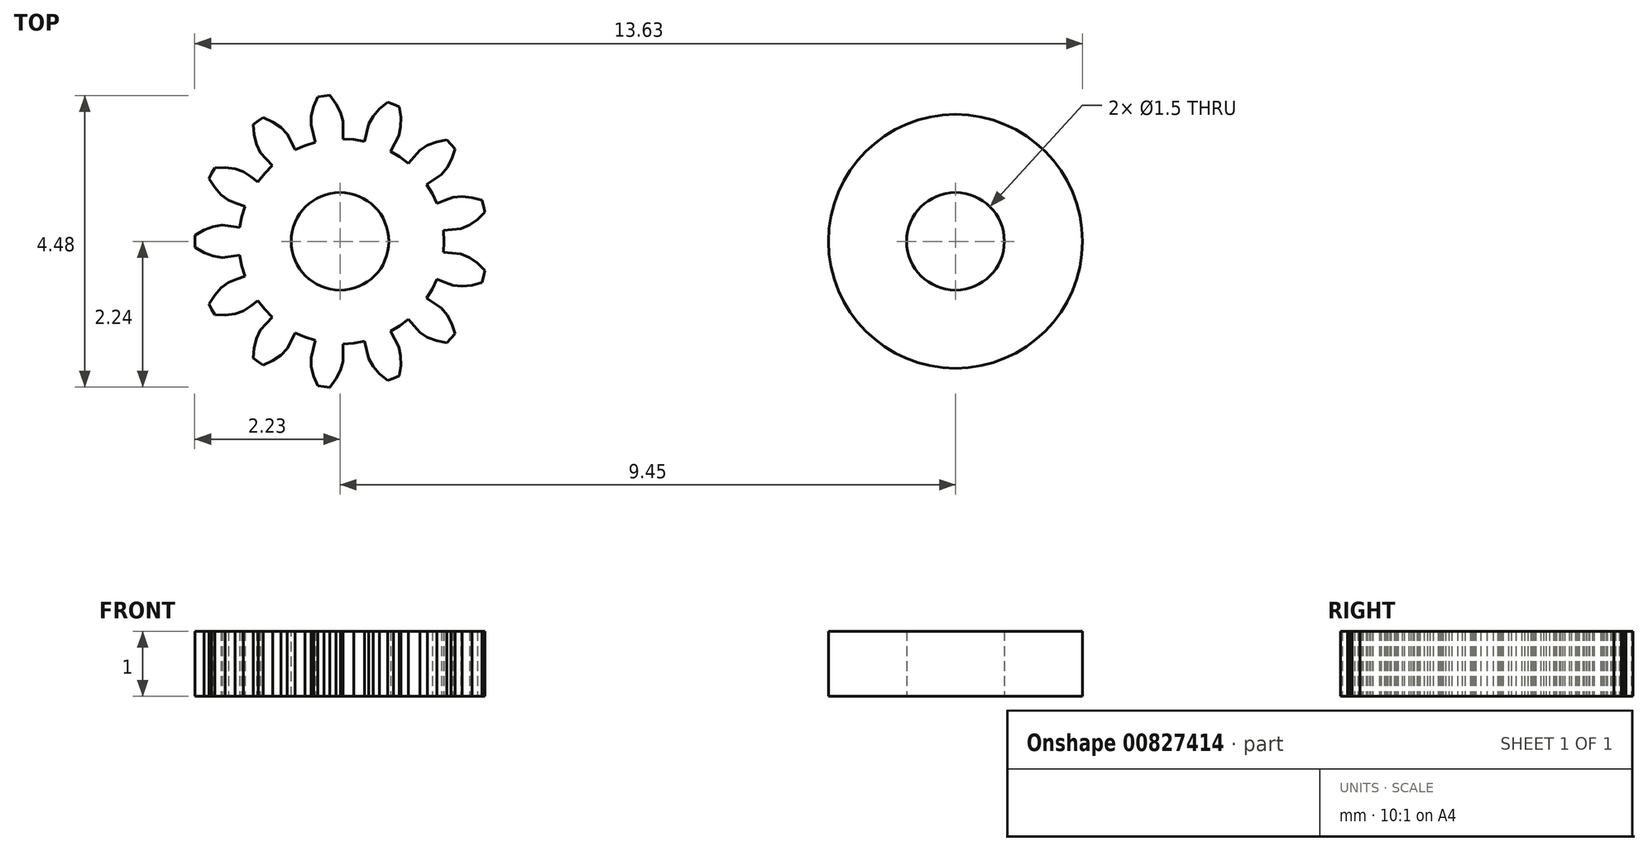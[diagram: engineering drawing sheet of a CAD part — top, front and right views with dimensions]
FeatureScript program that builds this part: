
annotation { "Feature Type Name" : "Feature", "Feature Type Description" : "" }
export const myFeature = defineFeature(function(context is Context, id is Id, definition is map)
    precondition{}
    {
        {
            var Q0;
            Q0=qCreatedBy(makeId("Top.planeOp"),FACE);
            var sketch = newSketch(context, id + "F0", { "sketchPlane" : qUnion([Q0])});
            skLineSegment(sketch, "E0", {"start": v(1.6, 0) * mm, "end": v(1.59, 0.17) * mm});
            skLineSegment(sketch, "E1", {"start": v(1.59, 0.17) * mm, "end": v(1.72, 0.18) * mm});
            skLineSegment(sketch, "E2", {"start": v(1.72, 0.18) * mm, "end": v(1.86, 0.2) * mm});
            skLineSegment(sketch, "E3", {"start": v(1.86, 0.2) * mm, "end": v(1.99, 0.25) * mm});
            skLineSegment(sketch, "E4", {"start": v(1.99, 0.25) * mm, "end": v(2.11, 0.34) * mm});
            skLineSegment(sketch, "E5", {"start": v(2.11, 0.34) * mm, "end": v(2.23, 0.45) * mm});
            skLineSegment(sketch, "E6", {"start": v(2.23, 0.45) * mm, "end": v(2.2, 0.54) * mm});
            skLineSegment(sketch, "E7", {"start": v(2.2, 0.54) * mm, "end": v(2.18, 0.63) * mm});
            skLineSegment(sketch, "E8", {"start": v(2.18, 0.63) * mm, "end": v(2.03, 0.67) * mm});
            skLineSegment(sketch, "E9", {"start": v(2.03, 0.67) * mm, "end": v(1.88, 0.7) * mm});
            skLineSegment(sketch, "E10", {"start": v(1.88, 0.7) * mm, "end": v(1.74, 0.68) * mm});
            skLineSegment(sketch, "E11", {"start": v(1.74, 0.68) * mm, "end": v(1.61, 0.63) * mm});
            skLineSegment(sketch, "E12", {"start": v(1.61, 0.63) * mm, "end": v(1.49, 0.58) * mm});
            skLineSegment(sketch, "E13", {"start": v(1.49, 0.58) * mm, "end": v(1.42, 0.73) * mm});
            skLineSegment(sketch, "E14", {"start": v(1.42, 0.73) * mm, "end": v(1.33, 0.88) * mm});
            skLineSegment(sketch, "E15", {"start": v(1.33, 0.88) * mm, "end": v(1.44, 0.95) * mm});
            skLineSegment(sketch, "E16", {"start": v(1.44, 0.95) * mm, "end": v(1.56, 1.03) * mm});
            skLineSegment(sketch, "E17", {"start": v(1.56, 1.03) * mm, "end": v(1.65, 1.13) * mm});
            skLineSegment(sketch, "E18", {"start": v(1.65, 1.13) * mm, "end": v(1.72, 1.27) * mm});
            skLineSegment(sketch, "E19", {"start": v(1.72, 1.27) * mm, "end": v(1.77, 1.42) * mm});
            skLineSegment(sketch, "E20", {"start": v(1.77, 1.42) * mm, "end": v(1.7, 1.5) * mm});
            skLineSegment(sketch, "E21", {"start": v(1.7, 1.5) * mm, "end": v(1.64, 1.56) * mm});
            skLineSegment(sketch, "E22", {"start": v(1.64, 1.56) * mm, "end": v(1.48, 1.53) * mm});
            skLineSegment(sketch, "E23", {"start": v(1.48, 1.53) * mm, "end": v(1.34, 1.47) * mm});
            skLineSegment(sketch, "E24", {"start": v(1.34, 1.47) * mm, "end": v(1.23, 1.4) * mm});
            skLineSegment(sketch, "E25", {"start": v(1.23, 1.4) * mm, "end": v(1.14, 1.3) * mm});
            skLineSegment(sketch, "E26", {"start": v(1.14, 1.3) * mm, "end": v(1.05, 1.2) * mm});
            skLineSegment(sketch, "E27", {"start": v(1.05, 1.2) * mm, "end": v(0.92, 1.3) * mm});
            skLineSegment(sketch, "E28", {"start": v(0.92, 1.3) * mm, "end": v(0.77, 1.38) * mm});
            skLineSegment(sketch, "E29", {"start": v(0.77, 1.38) * mm, "end": v(0.84, 1.5) * mm});
            skLineSegment(sketch, "E30", {"start": v(0.84, 1.5) * mm, "end": v(0.9, 1.62) * mm});
            skLineSegment(sketch, "E31", {"start": v(0.9, 1.62) * mm, "end": v(0.93, 1.76) * mm});
            skLineSegment(sketch, "E32", {"start": v(0.93, 1.76) * mm, "end": v(0.93, 1.9) * mm});
            skLineSegment(sketch, "E33", {"start": v(0.93, 1.9) * mm, "end": v(0.9, 2.07) * mm});
            skLineSegment(sketch, "E34", {"start": v(0.9, 2.07) * mm, "end": v(0.82, 2.1) * mm});
            skLineSegment(sketch, "E35", {"start": v(0.82, 2.1) * mm, "end": v(0.73, 2.14) * mm});
            skLineSegment(sketch, "E36", {"start": v(0.73, 2.14) * mm, "end": v(0.6, 2.03) * mm});
            skLineSegment(sketch, "E37", {"start": v(0.6, 2.03) * mm, "end": v(0.5, 1.92) * mm});
            skLineSegment(sketch, "E38", {"start": v(0.5, 1.92) * mm, "end": v(0.44, 1.8) * mm});
            skLineSegment(sketch, "E39", {"start": v(0.44, 1.8) * mm, "end": v(0.4, 1.67) * mm});
            skLineSegment(sketch, "E40", {"start": v(0.4, 1.67) * mm, "end": v(0.38, 1.53) * mm});
            skLineSegment(sketch, "E41", {"start": v(0.38, 1.53) * mm, "end": v(0.21, 1.56) * mm});
            skLineSegment(sketch, "E42", {"start": v(0.21, 1.56) * mm, "end": v(0.05, 1.57) * mm});
            skLineSegment(sketch, "E43", {"start": v(0.05, 1.57) * mm, "end": v(0.05, 1.7) * mm});
            skLineSegment(sketch, "E44", {"start": v(0.05, 1.7) * mm, "end": v(0.05, 1.84) * mm});
            skLineSegment(sketch, "E45", {"start": v(0.05, 1.84) * mm, "end": v(0.01, 1.98) * mm});
            skLineSegment(sketch, "E46", {"start": v(0.01, 1.98) * mm, "end": v(-0.06, 2.11) * mm});
            skLineSegment(sketch, "E47", {"start": v(-0.06, 2.11) * mm, "end": v(-0.15, 2.24) * mm});
            skLineSegment(sketch, "E48", {"start": v(-0.15, 2.24) * mm, "end": v(-0.25, 2.23) * mm});
            skLineSegment(sketch, "E49", {"start": v(-0.25, 2.23) * mm, "end": v(-0.34, 2.22) * mm});
            skLineSegment(sketch, "E50", {"start": v(-0.34, 2.22) * mm, "end": v(-0.4, 2.07) * mm});
            skLineSegment(sketch, "E51", {"start": v(-0.4, 2.07) * mm, "end": v(-0.44, 1.93) * mm});
            skLineSegment(sketch, "E52", {"start": v(-0.44, 1.93) * mm, "end": v(-0.44, 1.78) * mm});
            skLineSegment(sketch, "E53", {"start": v(-0.44, 1.78) * mm, "end": v(-0.41, 1.65) * mm});
            skLineSegment(sketch, "E54", {"start": v(-0.41, 1.65) * mm, "end": v(-0.38, 1.52) * mm});
            skLineSegment(sketch, "E55", {"start": v(-0.38, 1.52) * mm, "end": v(-0.54, 1.47) * mm});
            skLineSegment(sketch, "E56", {"start": v(-0.54, 1.47) * mm, "end": v(-0.69, 1.4) * mm});
            skLineSegment(sketch, "E57", {"start": v(-0.69, 1.4) * mm, "end": v(-0.75, 1.53) * mm});
            skLineSegment(sketch, "E58", {"start": v(-0.75, 1.53) * mm, "end": v(-0.81, 1.65) * mm});
            skLineSegment(sketch, "E59", {"start": v(-0.81, 1.65) * mm, "end": v(-0.9, 1.75) * mm});
            skLineSegment(sketch, "E60", {"start": v(-0.9, 1.75) * mm, "end": v(-1.03, 1.83) * mm});
            skLineSegment(sketch, "E61", {"start": v(-1.03, 1.83) * mm, "end": v(-1.18, 1.9) * mm});
            skLineSegment(sketch, "E62", {"start": v(-1.18, 1.9) * mm, "end": v(-1.26, 1.85) * mm});
            skLineSegment(sketch, "E63", {"start": v(-1.26, 1.85) * mm, "end": v(-1.33, 1.8) * mm});
            skLineSegment(sketch, "E64", {"start": v(-1.33, 1.8) * mm, "end": v(-1.32, 1.64) * mm});
            skLineSegment(sketch, "E65", {"start": v(-1.32, 1.64) * mm, "end": v(-1.28, 1.49) * mm});
            skLineSegment(sketch, "E66", {"start": v(-1.28, 1.49) * mm, "end": v(-1.22, 1.36) * mm});
            skLineSegment(sketch, "E67", {"start": v(-1.22, 1.36) * mm, "end": v(-1.13, 1.26) * mm});
            skLineSegment(sketch, "E68", {"start": v(-1.13, 1.26) * mm, "end": v(-1.04, 1.16) * mm});
            skLineSegment(sketch, "E69", {"start": v(-1.04, 1.16) * mm, "end": v(-1.16, 1.04) * mm});
            skLineSegment(sketch, "E70", {"start": v(-1.16, 1.04) * mm, "end": v(-1.26, 0.91) * mm});
            skLineSegment(sketch, "E71", {"start": v(-1.26, 0.91) * mm, "end": v(-1.37, 1) * mm});
            skLineSegment(sketch, "E72", {"start": v(-1.37, 1) * mm, "end": v(-1.48, 1.07) * mm});
            skLineSegment(sketch, "E73", {"start": v(-1.48, 1.07) * mm, "end": v(-1.61, 1.12) * mm});
            skLineSegment(sketch, "E74", {"start": v(-1.61, 1.12) * mm, "end": v(-1.76, 1.13) * mm});
            skLineSegment(sketch, "E75", {"start": v(-1.76, 1.13) * mm, "end": v(-1.92, 1.13) * mm});
            skLineSegment(sketch, "E76", {"start": v(-1.92, 1.13) * mm, "end": v(-1.97, 1.05) * mm});
            skLineSegment(sketch, "E77", {"start": v(-1.97, 1.05) * mm, "end": v(-2.01, 0.96) * mm});
            skLineSegment(sketch, "E78", {"start": v(-2.01, 0.96) * mm, "end": v(-1.92, 0.83) * mm});
            skLineSegment(sketch, "E79", {"start": v(-1.92, 0.83) * mm, "end": v(-1.82, 0.71) * mm});
            skLineSegment(sketch, "E80", {"start": v(-1.82, 0.71) * mm, "end": v(-1.71, 0.63) * mm});
            skLineSegment(sketch, "E81", {"start": v(-1.71, 0.63) * mm, "end": v(-1.59, 0.58) * mm});
            skLineSegment(sketch, "E82", {"start": v(-1.59, 0.58) * mm, "end": v(-1.46, 0.54) * mm});
            skLineSegment(sketch, "E83", {"start": v(-1.46, 0.54) * mm, "end": v(-1.5, 0.38) * mm});
            skLineSegment(sketch, "E84", {"start": v(-1.5, 0.38) * mm, "end": v(-1.54, 0.21) * mm});
            skLineSegment(sketch, "E85", {"start": v(-1.54, 0.21) * mm, "end": v(-1.67, 0.23) * mm});
            skLineSegment(sketch, "E86", {"start": v(-1.67, 0.23) * mm, "end": v(-1.8, 0.25) * mm});
            skLineSegment(sketch, "E87", {"start": v(-1.8, 0.25) * mm, "end": v(-1.94, 0.23) * mm});
            skLineSegment(sketch, "E88", {"start": v(-1.94, 0.23) * mm, "end": v(-2.09, 0.17) * mm});
            skLineSegment(sketch, "E89", {"start": v(-2.09, 0.17) * mm, "end": v(-2.23, 0.1) * mm});
            skLineSegment(sketch, "E90", {"start": v(-2.23, 0.1) * mm, "end": v(-2.23, 0) * mm});
            skLineSegment(sketch, "E91", {"start": v(-2.23, 0) * mm, "end": v(-2.23, -0.1) * mm});
            skLineSegment(sketch, "E92", {"start": v(-2.23, -0.1) * mm, "end": v(-2.09, -0.17) * mm});
            skLineSegment(sketch, "E93", {"start": v(-2.09, -0.17) * mm, "end": v(-1.94, -0.23) * mm});
            skLineSegment(sketch, "E94", {"start": v(-1.94, -0.23) * mm, "end": v(-1.8, -0.25) * mm});
            skLineSegment(sketch, "E95", {"start": v(-1.8, -0.25) * mm, "end": v(-1.67, -0.23) * mm});
            skLineSegment(sketch, "E96", {"start": v(-1.67, -0.23) * mm, "end": v(-1.54, -0.21) * mm});
            skLineSegment(sketch, "E97", {"start": v(-1.54, -0.21) * mm, "end": v(-1.5, -0.38) * mm});
            skLineSegment(sketch, "E98", {"start": v(-1.5, -0.38) * mm, "end": v(-1.46, -0.54) * mm});
            skLineSegment(sketch, "E99", {"start": v(-1.46, -0.54) * mm, "end": v(-1.59, -0.58) * mm});
            skLineSegment(sketch, "E100", {"start": v(-1.59, -0.58) * mm, "end": v(-1.71, -0.63) * mm});
            skLineSegment(sketch, "E101", {"start": v(-1.71, -0.63) * mm, "end": v(-1.82, -0.71) * mm});
            skLineSegment(sketch, "E102", {"start": v(-1.82, -0.71) * mm, "end": v(-1.92, -0.83) * mm});
            skLineSegment(sketch, "E103", {"start": v(-1.92, -0.83) * mm, "end": v(-2.01, -0.96) * mm});
            skLineSegment(sketch, "E104", {"start": v(-2.01, -0.96) * mm, "end": v(-1.97, -1.05) * mm});
            skLineSegment(sketch, "E105", {"start": v(-1.97, -1.05) * mm, "end": v(-1.92, -1.13) * mm});
            skLineSegment(sketch, "E106", {"start": v(-1.92, -1.13) * mm, "end": v(-1.76, -1.13) * mm});
            skLineSegment(sketch, "E107", {"start": v(-1.76, -1.13) * mm, "end": v(-1.61, -1.12) * mm});
            skLineSegment(sketch, "E108", {"start": v(-1.61, -1.12) * mm, "end": v(-1.48, -1.07) * mm});
            skLineSegment(sketch, "E109", {"start": v(-1.48, -1.07) * mm, "end": v(-1.37, -1) * mm});
            skLineSegment(sketch, "E110", {"start": v(-1.37, -1) * mm, "end": v(-1.26, -0.91) * mm});
            skLineSegment(sketch, "E111", {"start": v(-1.26, -0.91) * mm, "end": v(-1.16, -1.04) * mm});
            skLineSegment(sketch, "E112", {"start": v(-1.16, -1.04) * mm, "end": v(-1.04, -1.16) * mm});
            skLineSegment(sketch, "E113", {"start": v(-1.04, -1.16) * mm, "end": v(-1.13, -1.26) * mm});
            skLineSegment(sketch, "E114", {"start": v(-1.13, -1.26) * mm, "end": v(-1.22, -1.36) * mm});
            skLineSegment(sketch, "E115", {"start": v(-1.22, -1.36) * mm, "end": v(-1.28, -1.49) * mm});
            skLineSegment(sketch, "E116", {"start": v(-1.28, -1.49) * mm, "end": v(-1.32, -1.64) * mm});
            skLineSegment(sketch, "E117", {"start": v(-1.32, -1.64) * mm, "end": v(-1.33, -1.8) * mm});
            skLineSegment(sketch, "E118", {"start": v(-1.33, -1.8) * mm, "end": v(-1.26, -1.85) * mm});
            skLineSegment(sketch, "E119", {"start": v(-1.26, -1.85) * mm, "end": v(-1.18, -1.9) * mm});
            skLineSegment(sketch, "E120", {"start": v(-1.18, -1.9) * mm, "end": v(-1.03, -1.83) * mm});
            skLineSegment(sketch, "E121", {"start": v(-1.03, -1.83) * mm, "end": v(-0.9, -1.75) * mm});
            skLineSegment(sketch, "E122", {"start": v(-0.9, -1.75) * mm, "end": v(-0.81, -1.65) * mm});
            skLineSegment(sketch, "E123", {"start": v(-0.81, -1.65) * mm, "end": v(-0.75, -1.53) * mm});
            skLineSegment(sketch, "E124", {"start": v(-0.75, -1.53) * mm, "end": v(-0.69, -1.4) * mm});
            skLineSegment(sketch, "E125", {"start": v(-0.69, -1.4) * mm, "end": v(-0.54, -1.47) * mm});
            skLineSegment(sketch, "E126", {"start": v(-0.54, -1.47) * mm, "end": v(-0.38, -1.52) * mm});
            skLineSegment(sketch, "E127", {"start": v(-0.38, -1.52) * mm, "end": v(-0.41, -1.65) * mm});
            skLineSegment(sketch, "E128", {"start": v(-0.41, -1.65) * mm, "end": v(-0.44, -1.78) * mm});
            skLineSegment(sketch, "E129", {"start": v(-0.44, -1.78) * mm, "end": v(-0.44, -1.93) * mm});
            skLineSegment(sketch, "E130", {"start": v(-0.44, -1.93) * mm, "end": v(-0.4, -2.07) * mm});
            skLineSegment(sketch, "E131", {"start": v(-0.4, -2.07) * mm, "end": v(-0.34, -2.22) * mm});
            skLineSegment(sketch, "E132", {"start": v(-0.34, -2.22) * mm, "end": v(-0.25, -2.23) * mm});
            skLineSegment(sketch, "E133", {"start": v(-0.25, -2.23) * mm, "end": v(-0.15, -2.24) * mm});
            skLineSegment(sketch, "E134", {"start": v(-0.15, -2.24) * mm, "end": v(-0.06, -2.11) * mm});
            skLineSegment(sketch, "E135", {"start": v(-0.06, -2.11) * mm, "end": v(0.01, -1.98) * mm});
            skLineSegment(sketch, "E136", {"start": v(0.01, -1.98) * mm, "end": v(0.05, -1.84) * mm});
            skLineSegment(sketch, "E137", {"start": v(0.05, -1.84) * mm, "end": v(0.05, -1.7) * mm});
            skLineSegment(sketch, "E138", {"start": v(0.05, -1.7) * mm, "end": v(0.05, -1.57) * mm});
            skLineSegment(sketch, "E139", {"start": v(0.05, -1.57) * mm, "end": v(0.21, -1.56) * mm});
            skLineSegment(sketch, "E140", {"start": v(0.21, -1.56) * mm, "end": v(0.38, -1.53) * mm});
            skLineSegment(sketch, "E141", {"start": v(0.38, -1.53) * mm, "end": v(0.4, -1.67) * mm});
            skLineSegment(sketch, "E142", {"start": v(0.4, -1.67) * mm, "end": v(0.44, -1.8) * mm});
            skLineSegment(sketch, "E143", {"start": v(0.44, -1.8) * mm, "end": v(0.5, -1.92) * mm});
            skLineSegment(sketch, "E144", {"start": v(0.5, -1.92) * mm, "end": v(0.6, -2.03) * mm});
            skLineSegment(sketch, "E145", {"start": v(0.6, -2.03) * mm, "end": v(0.73, -2.14) * mm});
            skLineSegment(sketch, "E146", {"start": v(0.73, -2.14) * mm, "end": v(0.82, -2.1) * mm});
            skLineSegment(sketch, "E147", {"start": v(0.82, -2.1) * mm, "end": v(0.9, -2.07) * mm});
            skLineSegment(sketch, "E148", {"start": v(0.9, -2.07) * mm, "end": v(0.93, -1.9) * mm});
            skLineSegment(sketch, "E149", {"start": v(0.93, -1.9) * mm, "end": v(0.93, -1.76) * mm});
            skLineSegment(sketch, "E150", {"start": v(0.93, -1.76) * mm, "end": v(0.9, -1.62) * mm});
            skLineSegment(sketch, "E151", {"start": v(0.9, -1.62) * mm, "end": v(0.84, -1.5) * mm});
            skLineSegment(sketch, "E152", {"start": v(0.84, -1.5) * mm, "end": v(0.77, -1.38) * mm});
            skLineSegment(sketch, "E153", {"start": v(0.77, -1.38) * mm, "end": v(0.92, -1.3) * mm});
            skLineSegment(sketch, "E154", {"start": v(0.92, -1.3) * mm, "end": v(1.05, -1.2) * mm});
            skLineSegment(sketch, "E155", {"start": v(1.05, -1.2) * mm, "end": v(1.14, -1.3) * mm});
            skLineSegment(sketch, "E156", {"start": v(1.14, -1.3) * mm, "end": v(1.23, -1.4) * mm});
            skLineSegment(sketch, "E157", {"start": v(1.23, -1.4) * mm, "end": v(1.34, -1.47) * mm});
            skLineSegment(sketch, "E158", {"start": v(1.34, -1.47) * mm, "end": v(1.48, -1.53) * mm});
            skLineSegment(sketch, "E159", {"start": v(1.48, -1.53) * mm, "end": v(1.64, -1.56) * mm});
            skLineSegment(sketch, "E160", {"start": v(1.64, -1.56) * mm, "end": v(1.7, -1.5) * mm});
            skLineSegment(sketch, "E161", {"start": v(1.7, -1.5) * mm, "end": v(1.77, -1.42) * mm});
            skLineSegment(sketch, "E162", {"start": v(1.77, -1.42) * mm, "end": v(1.72, -1.27) * mm});
            skLineSegment(sketch, "E163", {"start": v(1.72, -1.27) * mm, "end": v(1.65, -1.13) * mm});
            skLineSegment(sketch, "E164", {"start": v(1.65, -1.13) * mm, "end": v(1.56, -1.03) * mm});
            skLineSegment(sketch, "E165", {"start": v(1.56, -1.03) * mm, "end": v(1.44, -0.95) * mm});
            skLineSegment(sketch, "E166", {"start": v(1.44, -0.95) * mm, "end": v(1.33, -0.88) * mm});
            skLineSegment(sketch, "E167", {"start": v(1.33, -0.88) * mm, "end": v(1.42, -0.73) * mm});
            skLineSegment(sketch, "E168", {"start": v(1.42, -0.73) * mm, "end": v(1.49, -0.58) * mm});
            skLineSegment(sketch, "E169", {"start": v(1.49, -0.58) * mm, "end": v(1.61, -0.63) * mm});
            skLineSegment(sketch, "E170", {"start": v(1.61, -0.63) * mm, "end": v(1.74, -0.68) * mm});
            skLineSegment(sketch, "E171", {"start": v(1.74, -0.68) * mm, "end": v(1.88, -0.7) * mm});
            skLineSegment(sketch, "E172", {"start": v(1.88, -0.7) * mm, "end": v(2.03, -0.67) * mm});
            skLineSegment(sketch, "E173", {"start": v(2.03, -0.67) * mm, "end": v(2.18, -0.63) * mm});
            skLineSegment(sketch, "E174", {"start": v(2.18, -0.63) * mm, "end": v(2.2, -0.54) * mm});
            skLineSegment(sketch, "E175", {"start": v(2.2, -0.54) * mm, "end": v(2.23, -0.45) * mm});
            skLineSegment(sketch, "E176", {"start": v(2.23, -0.45) * mm, "end": v(2.11, -0.34) * mm});
            skLineSegment(sketch, "E177", {"start": v(2.11, -0.34) * mm, "end": v(1.99, -0.25) * mm});
            skLineSegment(sketch, "E178", {"start": v(1.99, -0.25) * mm, "end": v(1.86, -0.2) * mm});
            skLineSegment(sketch, "E179", {"start": v(1.86, -0.2) * mm, "end": v(1.72, -0.18) * mm});
            skLineSegment(sketch, "E180", {"start": v(1.72, -0.18) * mm, "end": v(1.59, -0.17) * mm});
            skLineSegment(sketch, "E181", {"start": v(1.6, 0) * mm, "end": v(1.59, -0.17) * mm});
            skSolve(sketch);
        }
        {
            var Q0;
            Q0 = qSketchRegion(id + "F0", true);
            extrude(context, id + "F1", {"entities" : qUnion([Q0]), "depth" : 1 * mm, "offsetDistance" : 25 * mm});
        }
        {
            var Q0;
            Q0=makeQuery(id+"F1.opExtrude","CAP_FACE",FACE,{"disambiguationData":[OSD([sQuery(id+"F0.wireOp",EDGE,"E0"),sQuery(id+"F0.wireOp",EDGE,"E1"),sQuery(id+"F0.wireOp",EDGE,"E2"),sQuery(id+"F0.wireOp",EDGE,"E3"),sQuery(id+"F0.wireOp",EDGE,"E4"),sQuery(id+"F0.wireOp",EDGE,"E5"),sQuery(id+"F0.wireOp",EDGE,"E6"),sQuery(id+"F0.wireOp",EDGE,"E7"),sQuery(id+"F0.wireOp",EDGE,"E8"),sQuery(id+"F0.wireOp",EDGE,"E9"),sQuery(id+"F0.wireOp",EDGE,"E10"),sQuery(id+"F0.wireOp",EDGE,"E11"),sQuery(id+"F0.wireOp",EDGE,"E12"),sQuery(id+"F0.wireOp",EDGE,"E13"),sQuery(id+"F0.wireOp",EDGE,"E14"),sQuery(id+"F0.wireOp",EDGE,"E15"),sQuery(id+"F0.wireOp",EDGE,"E16"),sQuery(id+"F0.wireOp",EDGE,"E17"),sQuery(id+"F0.wireOp",EDGE,"E18"),sQuery(id+"F0.wireOp",EDGE,"E19"),sQuery(id+"F0.wireOp",EDGE,"E20"),sQuery(id+"F0.wireOp",EDGE,"E21"),sQuery(id+"F0.wireOp",EDGE,"E22"),sQuery(id+"F0.wireOp",EDGE,"E23"),sQuery(id+"F0.wireOp",EDGE,"E24"),sQuery(id+"F0.wireOp",EDGE,"E25"),sQuery(id+"F0.wireOp",EDGE,"E26"),sQuery(id+"F0.wireOp",EDGE,"E27"),sQuery(id+"F0.wireOp",EDGE,"E28"),sQuery(id+"F0.wireOp",EDGE,"E29"),sQuery(id+"F0.wireOp",EDGE,"E30"),sQuery(id+"F0.wireOp",EDGE,"E31"),sQuery(id+"F0.wireOp",EDGE,"E32"),sQuery(id+"F0.wireOp",EDGE,"E33"),sQuery(id+"F0.wireOp",EDGE,"E34"),sQuery(id+"F0.wireOp",EDGE,"E35"),sQuery(id+"F0.wireOp",EDGE,"E36"),sQuery(id+"F0.wireOp",EDGE,"E37"),sQuery(id+"F0.wireOp",EDGE,"E38"),sQuery(id+"F0.wireOp",EDGE,"E39"),sQuery(id+"F0.wireOp",EDGE,"E40"),sQuery(id+"F0.wireOp",EDGE,"E41"),sQuery(id+"F0.wireOp",EDGE,"E42"),sQuery(id+"F0.wireOp",EDGE,"E43"),sQuery(id+"F0.wireOp",EDGE,"E44"),sQuery(id+"F0.wireOp",EDGE,"E45"),sQuery(id+"F0.wireOp",EDGE,"E46"),sQuery(id+"F0.wireOp",EDGE,"E47"),sQuery(id+"F0.wireOp",EDGE,"E48"),sQuery(id+"F0.wireOp",EDGE,"E49"),sQuery(id+"F0.wireOp",EDGE,"E50"),sQuery(id+"F0.wireOp",EDGE,"E51"),sQuery(id+"F0.wireOp",EDGE,"E52"),sQuery(id+"F0.wireOp",EDGE,"E53"),sQuery(id+"F0.wireOp",EDGE,"E54"),sQuery(id+"F0.wireOp",EDGE,"E55"),sQuery(id+"F0.wireOp",EDGE,"E56"),sQuery(id+"F0.wireOp",EDGE,"E57"),sQuery(id+"F0.wireOp",EDGE,"E58"),sQuery(id+"F0.wireOp",EDGE,"E59"),sQuery(id+"F0.wireOp",EDGE,"E60"),sQuery(id+"F0.wireOp",EDGE,"E61"),sQuery(id+"F0.wireOp",EDGE,"E62"),sQuery(id+"F0.wireOp",EDGE,"E63"),sQuery(id+"F0.wireOp",EDGE,"E64"),sQuery(id+"F0.wireOp",EDGE,"E65"),sQuery(id+"F0.wireOp",EDGE,"E66"),sQuery(id+"F0.wireOp",EDGE,"E67"),sQuery(id+"F0.wireOp",EDGE,"E68"),sQuery(id+"F0.wireOp",EDGE,"E69"),sQuery(id+"F0.wireOp",EDGE,"E70"),sQuery(id+"F0.wireOp",EDGE,"E71"),sQuery(id+"F0.wireOp",EDGE,"E72"),sQuery(id+"F0.wireOp",EDGE,"E73"),sQuery(id+"F0.wireOp",EDGE,"E74"),sQuery(id+"F0.wireOp",EDGE,"E75"),sQuery(id+"F0.wireOp",EDGE,"E76"),sQuery(id+"F0.wireOp",EDGE,"E77"),sQuery(id+"F0.wireOp",EDGE,"E78"),sQuery(id+"F0.wireOp",EDGE,"E79"),sQuery(id+"F0.wireOp",EDGE,"E80"),sQuery(id+"F0.wireOp",EDGE,"E81"),sQuery(id+"F0.wireOp",EDGE,"E82"),sQuery(id+"F0.wireOp",EDGE,"E83"),sQuery(id+"F0.wireOp",EDGE,"E84"),sQuery(id+"F0.wireOp",EDGE,"E85"),sQuery(id+"F0.wireOp",EDGE,"E86"),sQuery(id+"F0.wireOp",EDGE,"E87"),sQuery(id+"F0.wireOp",EDGE,"E88"),sQuery(id+"F0.wireOp",EDGE,"E89"),sQuery(id+"F0.wireOp",EDGE,"E90"),sQuery(id+"F0.wireOp",EDGE,"E91"),sQuery(id+"F0.wireOp",EDGE,"E92"),sQuery(id+"F0.wireOp",EDGE,"E93"),sQuery(id+"F0.wireOp",EDGE,"E94"),sQuery(id+"F0.wireOp",EDGE,"E95"),sQuery(id+"F0.wireOp",EDGE,"E96"),sQuery(id+"F0.wireOp",EDGE,"E97"),sQuery(id+"F0.wireOp",EDGE,"E98"),sQuery(id+"F0.wireOp",EDGE,"E99"),sQuery(id+"F0.wireOp",EDGE,"E100"),sQuery(id+"F0.wireOp",EDGE,"E101"),sQuery(id+"F0.wireOp",EDGE,"E102"),sQuery(id+"F0.wireOp",EDGE,"E103"),sQuery(id+"F0.wireOp",EDGE,"E104"),sQuery(id+"F0.wireOp",EDGE,"E105"),sQuery(id+"F0.wireOp",EDGE,"E106"),sQuery(id+"F0.wireOp",EDGE,"E107"),sQuery(id+"F0.wireOp",EDGE,"E108"),sQuery(id+"F0.wireOp",EDGE,"E109"),sQuery(id+"F0.wireOp",EDGE,"E110"),sQuery(id+"F0.wireOp",EDGE,"E111"),sQuery(id+"F0.wireOp",EDGE,"E112"),sQuery(id+"F0.wireOp",EDGE,"E113"),sQuery(id+"F0.wireOp",EDGE,"E114"),sQuery(id+"F0.wireOp",EDGE,"E115"),sQuery(id+"F0.wireOp",EDGE,"E116"),sQuery(id+"F0.wireOp",EDGE,"E117"),sQuery(id+"F0.wireOp",EDGE,"E118"),sQuery(id+"F0.wireOp",EDGE,"E119"),sQuery(id+"F0.wireOp",EDGE,"E120"),sQuery(id+"F0.wireOp",EDGE,"E121"),sQuery(id+"F0.wireOp",EDGE,"E122"),sQuery(id+"F0.wireOp",EDGE,"E123"),sQuery(id+"F0.wireOp",EDGE,"E124"),sQuery(id+"F0.wireOp",EDGE,"E125"),sQuery(id+"F0.wireOp",EDGE,"E126"),sQuery(id+"F0.wireOp",EDGE,"E127"),sQuery(id+"F0.wireOp",EDGE,"E128"),sQuery(id+"F0.wireOp",EDGE,"E129"),sQuery(id+"F0.wireOp",EDGE,"E130"),sQuery(id+"F0.wireOp",EDGE,"E131"),sQuery(id+"F0.wireOp",EDGE,"E132"),sQuery(id+"F0.wireOp",EDGE,"E133"),sQuery(id+"F0.wireOp",EDGE,"E134"),sQuery(id+"F0.wireOp",EDGE,"E135"),sQuery(id+"F0.wireOp",EDGE,"E136"),sQuery(id+"F0.wireOp",EDGE,"E137"),sQuery(id+"F0.wireOp",EDGE,"E138"),sQuery(id+"F0.wireOp",EDGE,"E139"),sQuery(id+"F0.wireOp",EDGE,"E140"),sQuery(id+"F0.wireOp",EDGE,"E141"),sQuery(id+"F0.wireOp",EDGE,"E142"),sQuery(id+"F0.wireOp",EDGE,"E143"),sQuery(id+"F0.wireOp",EDGE,"E144"),sQuery(id+"F0.wireOp",EDGE,"E145"),sQuery(id+"F0.wireOp",EDGE,"E146"),sQuery(id+"F0.wireOp",EDGE,"E147"),sQuery(id+"F0.wireOp",EDGE,"E148"),sQuery(id+"F0.wireOp",EDGE,"E149"),sQuery(id+"F0.wireOp",EDGE,"E150"),sQuery(id+"F0.wireOp",EDGE,"E151"),sQuery(id+"F0.wireOp",EDGE,"E152"),sQuery(id+"F0.wireOp",EDGE,"E153"),sQuery(id+"F0.wireOp",EDGE,"E154"),sQuery(id+"F0.wireOp",EDGE,"E155"),sQuery(id+"F0.wireOp",EDGE,"E156"),sQuery(id+"F0.wireOp",EDGE,"E157"),sQuery(id+"F0.wireOp",EDGE,"E158"),sQuery(id+"F0.wireOp",EDGE,"E159"),sQuery(id+"F0.wireOp",EDGE,"E160"),sQuery(id+"F0.wireOp",EDGE,"E161"),sQuery(id+"F0.wireOp",EDGE,"E162"),sQuery(id+"F0.wireOp",EDGE,"E163"),sQuery(id+"F0.wireOp",EDGE,"E164"),sQuery(id+"F0.wireOp",EDGE,"E165"),sQuery(id+"F0.wireOp",EDGE,"E166"),sQuery(id+"F0.wireOp",EDGE,"E167"),sQuery(id+"F0.wireOp",EDGE,"E168"),sQuery(id+"F0.wireOp",EDGE,"E169"),sQuery(id+"F0.wireOp",EDGE,"E170"),sQuery(id+"F0.wireOp",EDGE,"E171"),sQuery(id+"F0.wireOp",EDGE,"E172"),sQuery(id+"F0.wireOp",EDGE,"E173"),sQuery(id+"F0.wireOp",EDGE,"E174"),sQuery(id+"F0.wireOp",EDGE,"E175"),sQuery(id+"F0.wireOp",EDGE,"E176"),sQuery(id+"F0.wireOp",EDGE,"E177"),sQuery(id+"F0.wireOp",EDGE,"E178"),sQuery(id+"F0.wireOp",EDGE,"E179"),sQuery(id+"F0.wireOp",EDGE,"E180"),sQuery(id+"F0.wireOp",EDGE,"E181")])],"isStart":false});
            var sketch = newSketch(context, id + "F2", { "sketchPlane" : qUnion([Q0])});
            skCircle(sketch, "E182", {"center": v(0, 0) * mm, "radius": 0.75 * mm});
            skSolve(sketch);
        }
        {
            var Q0;
            Q0=makeQuery(id+"F2.imprint","IMPRINT",FACE,{"disambiguationData":[TD([[makeQuery(id+"F2.imprint","IMPRINT",EDGE,{"derivedFrom":sQuery(id+"F2.wireOp",EDGE,"E182")}),1.0]])]});
            extrude(context, id + "F3", {"entities" : qUnion([Q0]), "operationType" : NewBodyOperationType.REMOVE, "oppositeDirection" : true, "depth" : 25 * mm, "offsetDistance" : 25 * mm});
        }
        {
            var Q0;
            Q0=qCreatedBy(makeId("Top.planeOp"),FACE);
            var sketch = newSketch(context, id + "F4", { "sketchPlane" : qUnion([Q0])});
            skCircle(sketch, "E183", {"center": v(9.45, 0) * mm, "radius": 1.95 * mm});
            skCircle(sketch, "E184", {"center": v(9.45, 0) * mm, "radius": 0.75 * mm});
            skSolve(sketch);
        }
        {
            var Q0;
            Q0=makeQuery(id+"F4.imprint","IMPRINT",FACE,{"disambiguationData":[TD([[makeQuery(id+"F4.imprint","IMPRINT",EDGE,{"derivedFrom":sQuery(id+"F4.wireOp",EDGE,"E183")}),1.0]])]});
            extrude(context, id + "F5", {"entities" : qUnion([Q0]), "depth" : 1 * mm, "offsetDistance" : 25 * mm});
        }
    });
